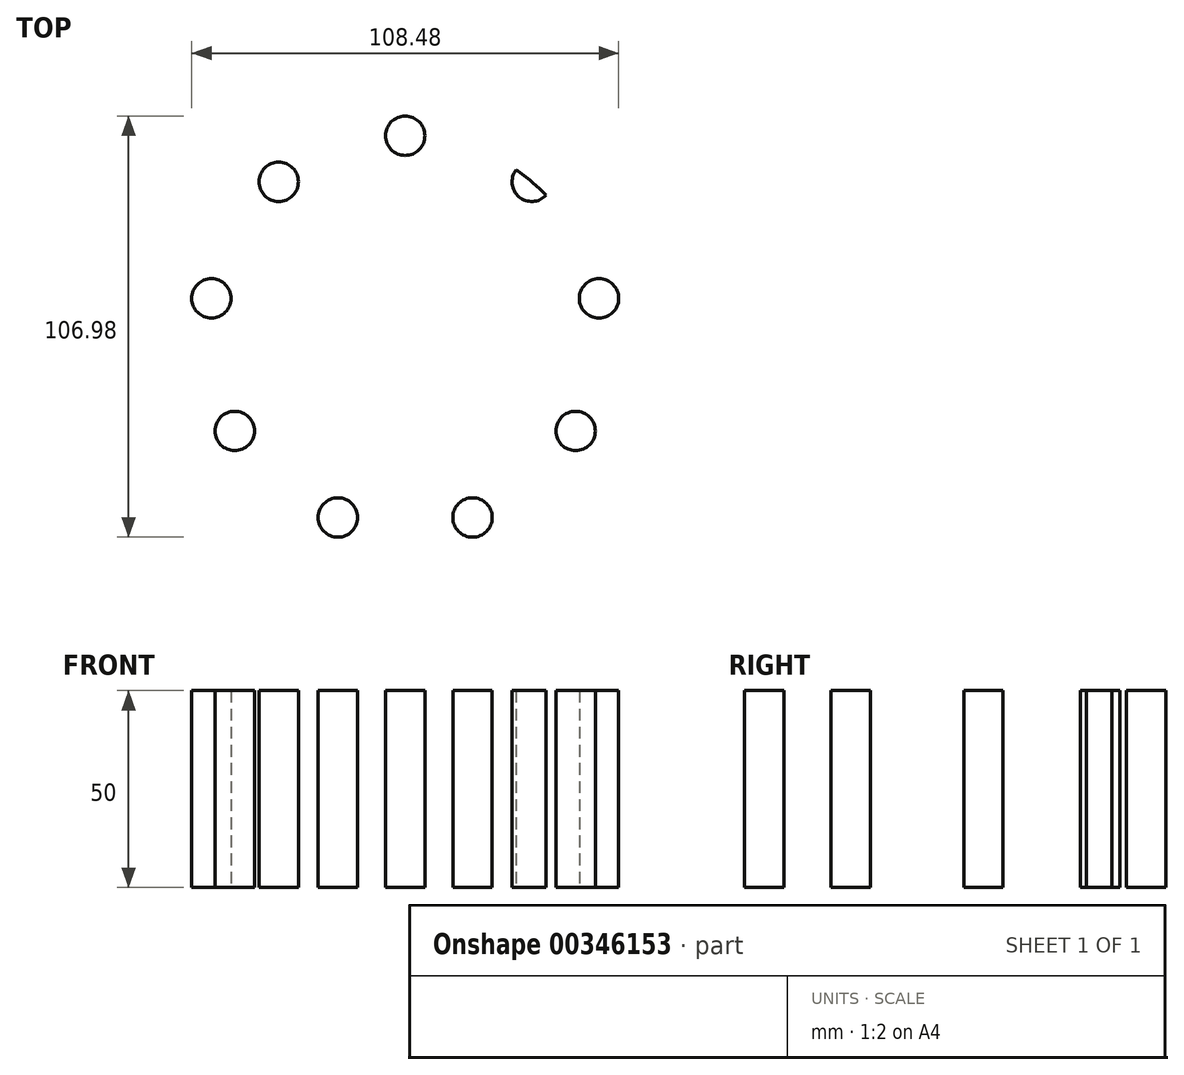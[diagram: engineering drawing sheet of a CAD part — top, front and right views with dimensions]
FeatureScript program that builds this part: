
annotation { "Feature Type Name" : "Feature", "Feature Type Description" : "" }
export const myFeature = defineFeature(function(context is Context, id is Id, definition is map)
    precondition{}
    {
        {
            var Q0;
            Q0=qCreatedBy(makeId("Top.planeOp"),FACE);
            var sketch = newSketch(context, id + "F0", { "sketchPlane" : qUnion([Q0])});
            skPoint(sketch, "E0.middle", {"position": v(0, 0) * mm});
            skCircle(sketch, "E1", {"center": v(0, 0) * mm, "radius": 50 * mm});
            skSolve(sketch);
        }
        {
            var Q0;
            Q0=makeQuery(id+"F0.imprint","IMPRINT",FACE,{"disambiguationData":[TD([[makeQuery(id+"F0.imprint","IMPRINT",EDGE,{"derivedFrom":sQuery(id+"F0.wireOp",EDGE,"E1")}),1.0]])]});
            extrude(context, id + "F1", {"entities" : qUnion([Q0]), "depth" : 50 * mm});
        }
        {
            var Q0;
            Q0=qCreatedBy(makeId("Top.planeOp"),FACE);
            var sketch = newSketch(context, id + "F2", { "sketchPlane" : qUnion([Q0])});
            skCircle(sketch, "E2", {"center": v(0, 0) * mm, "radius": 50 * mm, "construction": true});
            skCircle(sketch, "E3", {"center": v(0, 50) * mm, "radius": 5 * mm});
            skCircle(sketch, "E4.1.0", {"center": v(-32.14, 38.3) * mm, "radius": 5 * mm});
            skCircle(sketch, "E4.2.0", {"center": v(-49.24, 8.68) * mm, "radius": 5 * mm});
            skCircle(sketch, "E4.3.0", {"center": v(-43.3, -25) * mm, "radius": 5 * mm});
            skCircle(sketch, "E4.4.0", {"center": v(-17.1, -46.98) * mm, "radius": 5 * mm});
            skCircle(sketch, "E4.5.0", {"center": v(17.1, -46.98) * mm, "radius": 5 * mm});
            skCircle(sketch, "E4.6.0", {"center": v(43.3, -25) * mm, "radius": 5 * mm});
            skCircle(sketch, "E4.7.0", {"center": v(49.24, 8.68) * mm, "radius": 5 * mm});
            skCircle(sketch, "E4.8.0", {"center": v(32.14, 38.3) * mm, "radius": 5 * mm});
            skSolve(sketch);
        }
        {
            var Q0;
            Q0 = qSketchRegion(id + "F2", true);
            var Q1;
            Q1=makeQuery(id+"F1.opExtrude","CAP_FACE",FACE,{"disambiguationData":[OSD([sQuery(id+"F0.wireOp",EDGE,"E1")])],"isStart":false});
            extrude(context, id + "F3", {"entities" : qUnion([Q0]), "endBound" : BoundingType.UP_TO_SURFACE, "endBoundEntityFace" : qUnion([Q1]), "depth" : 25 * mm});
        }
        {
            var Q0;
            Q0=makeQuery(id+"F3.opExtrude","SWEPT_BODY",BODY,{"disambiguationData":[OSD([sQuery(id+"F2.wireOp",EDGE,"E4.8.0")])]});
            var Q1;
            Q1=makeQuery(id+"F1.opExtrude","SWEPT_BODY",BODY,{"disambiguationData":[OSD([sQuery(id+"F0.wireOp",EDGE,"E1")])]});
            var Q2;
            Q2=makeQuery(id+"F1.opExtrude","SWEPT_BODY",BODY,{"disambiguationData":[OSD([sQuery(id+"F0.wireOp",EDGE,"E1")])]});
            booleanBodies(context, id + "F4", {"operationType" : BooleanOperationType.INTERSECTION, "tools" : qUnion([Q0, Q1]), "targets" : qUnion([Q2])});
        }
    });
